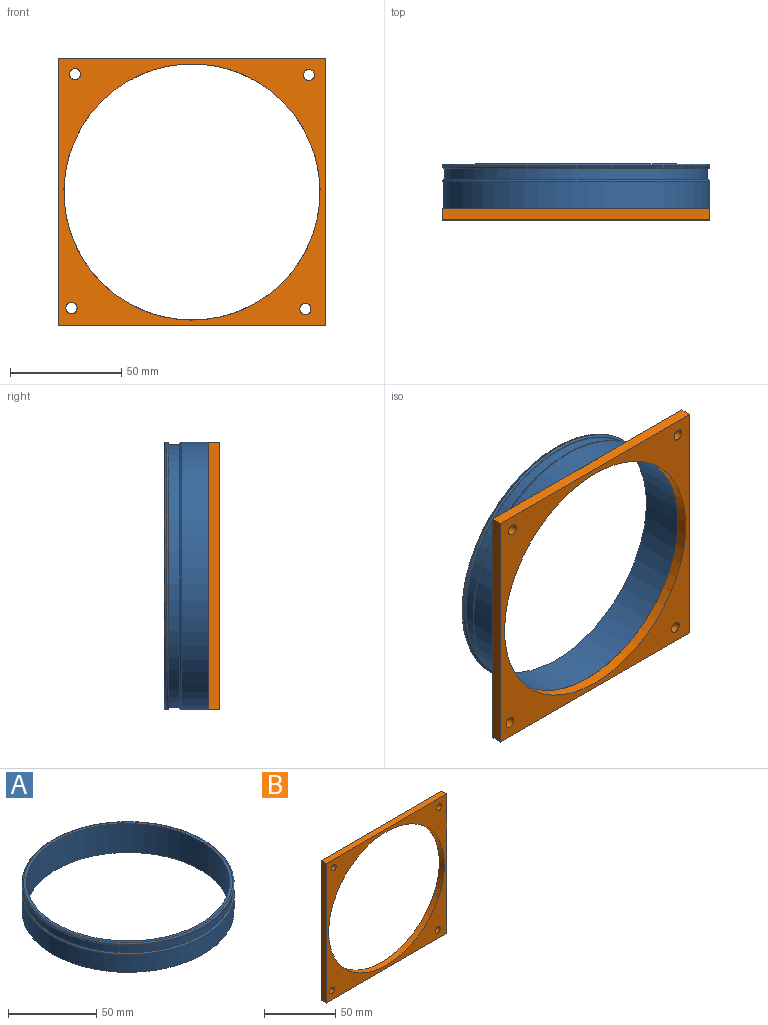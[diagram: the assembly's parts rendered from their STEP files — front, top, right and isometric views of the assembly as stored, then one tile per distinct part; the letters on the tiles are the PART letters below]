
ASSEMBLY  parts=2 mates=1
PART A: 11 faces, bbox 129.9x129.9x20 mm
  f0: torus R=59.17mm, axis (0,0,1), area 490.4mm2, adj f1,f10
  f1: plane 118.34x118.34mm, normal (0,0,-1), area 62.3mm2, adj f0,f2
  f2: cylinder r=59mm len=118mm, axis (0,0,1), area 1853.5mm2, adj f1,f3
  f3: plane 118.34x118.34mm, normal (0,0,1), area 62.4mm2, adj f2,f4
  f4: torus R=59.17mm, axis (0,0,1), area 490.2mm2, adj f3,f5
  f5: cylinder r=60mm len=120mm, axis (0,0,1), area 4587.2mm2, adj f4,f6
  f6: plane 120x120mm, normal (0,0,-1), area 922.8mm2, adj f5,f7
  f7: cylinder r=57.5mm len=115mm, axis (0,0,1), area 7225.7mm2, adj f6,f8
  f8: plane 118.34x118.34mm, normal (0,0,1), area 611.4mm2, adj f7,f9
  f9: torus R=59.17mm, axis (0,0,1), area 490.2mm2, adj f8,f10
  f10: cylinder r=60mm len=120mm, axis (0,0,1), area 126.6mm2, adj f0,f9
PART B: 11 faces, bbox 120x5x120 mm
  f0: plane 120x5mm, normal (0,0,-1), area 600mm2, adj f1,f4,f5,f6
  f1: plane 120x5mm, normal (1,0,0), area 600mm2, adj f0,f2,f5,f6
  f2: plane 120x5mm, normal (0,0,1), area 600mm2, adj f1,f4,f5,f6
  f3: cylinder r=57.5mm len=115mm, axis (0,-1,0), area 1806.4mm2, adj f5,f6
  f4: plane 120x5mm, normal (-1,0,0), area 600mm2, adj f0,f2,f5,f6
  f5: plane 120x120mm, normal (0,-1,0), area 3934.6mm2, adj f0,f1,f2,f3,f4,f7,f8,f9
  f6: plane 120x120mm, normal (0,1,0), area 3934.6mm2, adj f0,f1,f2,f3,f4,f7,f8,f9
  f7: cylinder r=2.5mm len=5mm, axis (0,1,0), area 78.5mm2, adj f5,f6
  f8: cylinder r=2.5mm len=5mm, axis (0,1,0), area 78.5mm2, adj f5,f6
  f9: cylinder r=2.5mm len=5mm, axis (0,1,0), area 78.5mm2, adj f5,f6
  f10: cylinder r=2.5mm len=5mm, axis (0,1,0), area 78.5mm2, adj f5,f6
PLACE A rot(axis=(-1,0,0),90deg) t=(17.3,-27.17,0)mm
PLACE B t=(-109.98,0,-12.85)mm
MATE fastened A.f2 <-> B.f3  axis (0,-1,0) through (1.45,0,0)mm
